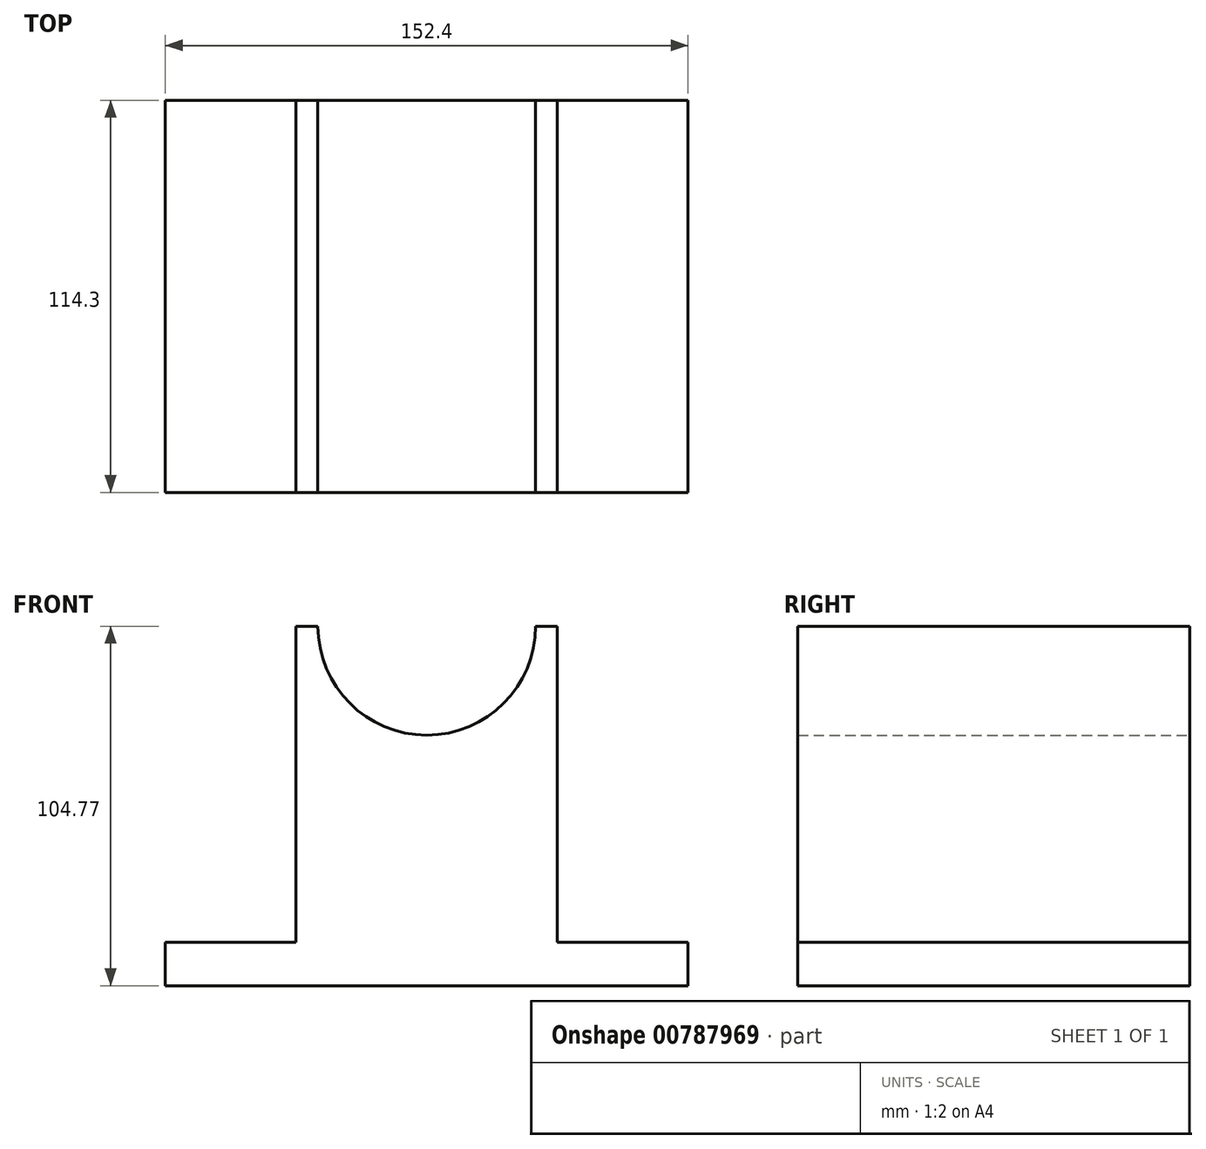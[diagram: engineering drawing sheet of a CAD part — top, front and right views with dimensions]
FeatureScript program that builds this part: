
annotation { "Feature Type Name" : "Feature", "Feature Type Description" : "" }
export const myFeature = defineFeature(function(context is Context, id is Id, definition is map)
    precondition{}
    {
        {
            var Q0;
            Q0=qCreatedBy(makeId("Front.planeOp"),FACE);
            var sketch = newSketch(context, id + "F0", { "sketchPlane" : qUnion([Q0])});
            skLineSegment(sketch, "E0", {"start": v(0, 0) * mm, "end": v(152.4, 0) * mm});
            skLineSegment(sketch, "E1", {"start": v(152.4, 0) * mm, "end": v(152.4, 12.7) * mm});
            skLineSegment(sketch, "E2", {"start": v(152.4, 12.7) * mm, "end": v(114.3, 12.7) * mm});
            skLineSegment(sketch, "E3", {"start": v(114.3, 12.7) * mm, "end": v(114.3, 104.78) * mm});
            skLineSegment(sketch, "E4", {"start": v(114.3, 104.78) * mm, "end": v(38.1, 104.78) * mm});
            skLineSegment(sketch, "E5", {"start": v(38.1, 104.78) * mm, "end": v(76.2, 104.78) * mm});
            skLineSegment(sketch, "E6", {"start": v(38.1, 104.78) * mm, "end": v(38.1, 12.7) * mm});
            skLineSegment(sketch, "E7", {"start": v(38.1, 12.7) * mm, "end": v(0, 12.7) * mm});
            skLineSegment(sketch, "E8", {"start": v(0, 12.7) * mm, "end": v(0, 0) * mm});
            skArc(sketch, "E9", {"start": v(107.95, 104.77) * mm, "mid": v(76.2, 73.03) * mm, "end": v(44.45, 104.78) * mm});
            skSolve(sketch);
        }
        {
            var Q0;
            Q0=makeQuery(id+"F0.imprint","IMPRINT",FACE,{"disambiguationData":[TD([[makeQuery(id+"F0.imprint","IMPRINT",EDGE,{"derivedFrom":sQuery(id+"F0.wireOp",EDGE,"E0")}),1.0]])]});
            extrude(context, id + "F1", {"entities" : qUnion([Q0]), "depth" : 114.3 * mm, "offsetDistance" : 25.4 * mm});
        }
    });
